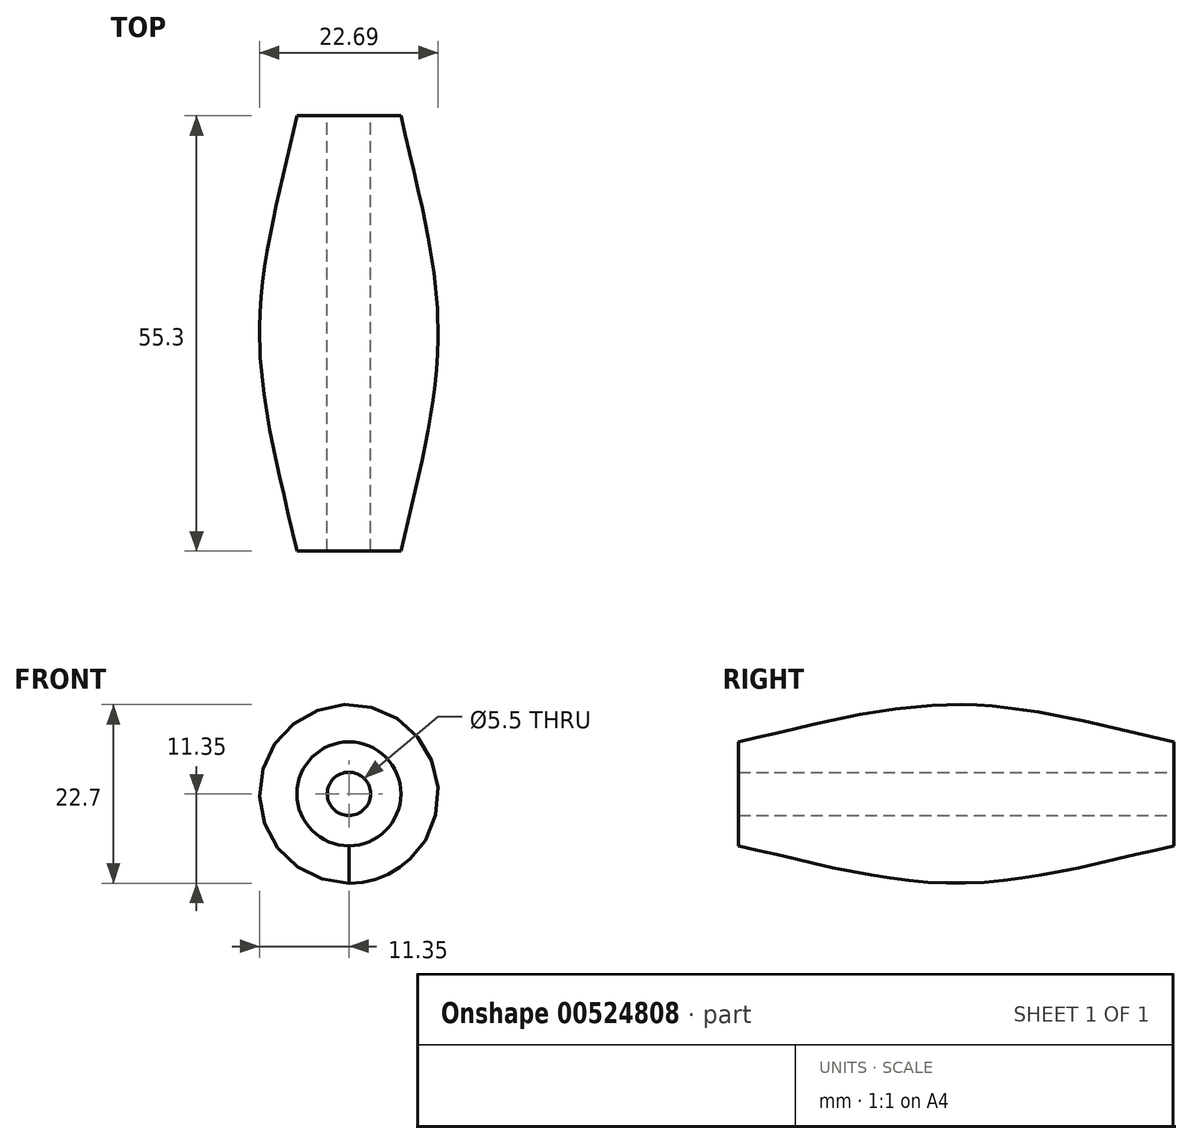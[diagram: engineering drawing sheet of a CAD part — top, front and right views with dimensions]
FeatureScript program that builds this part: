
annotation { "Feature Type Name" : "Feature", "Feature Type Description" : "" }
export const myFeature = defineFeature(function(context is Context, id is Id, definition is map)
    precondition{}
    {
        {
            assignVariable(context, id + "F0", {"name" : "length", "anyValue" : 55.3});
        }
        {
            var Q0;
            Q0=qCreatedBy(makeId("Front.planeOp"),FACE);
            var sketch = newSketch(context, id + "F1", { "sketchPlane" : qUnion([Q0])});
            skCircle(sketch, "E0", {"center": v(0, 0) * mm, "radius": 2.75 * mm});
            skSolve(sketch);
        }
        {
            var Q0;
            Q0=qCreatedBy(makeId("Right.planeOp"),FACE);
            var sketch = newSketch(context, id + "F2", { "sketchPlane" : qUnion([Q0])});
            skLineSegment(sketch, "E1.bottom", {"start": v(27.65, 6.6) * mm, "end": v(-27.65, 6.6) * mm});
            skLineSegment(sketch, "E1.top", {"start": v(27.65, -6.6) * mm, "end": v(-27.65, -6.6) * mm});
            skLineSegment(sketch, "E1.left", {"start": v(27.65, 6.6) * mm, "end": v(27.65, -6.6) * mm});
            skLineSegment(sketch, "E1.right", {"start": v(-27.65, 6.6) * mm, "end": v(-27.65, -6.6) * mm});
            skPoint(sketch, "E1.middle", {"position": v(0, 0) * mm});
            skFitSpline(sketch, "E2", {"points": [v(27.65, 6.6) * mm, v(0, 11.35) * mm, v(-27.65, 6.6) * mm], "startDerivative": vector(-55.3, 12.48) * mm, "endDerivative": vector(-55.3, -12.48) * mm});
            skLineSegment(sketch, "E3", {"start": v(-64.67, 0) * mm, "end": v(60.55, 0) * mm});
            skSolve(sketch);
        }
        {
            var Q0;
            Q0=makeQuery(id+"F2.imprint","IMPRINT",FACE,{"disambiguationData":[TD([[makeQuery(id+"F2.imprint","IMPRINT",EDGE,{"derivedFrom":sQuery(id+"F2.wireOp",EDGE,"E1.bottom")}),-1.0]])]});
            var Q1;
            {var subQ0=sQuery(id+"F2.wireOp",EDGE,"E1.bottom");Q1=makeQuery(id+"F2.imprint","IMPRINT",FACE,{"disambiguationData":[TD([[makeQuery(id+"F2.imprint","IMPRINT",EDGE,{"derivedFrom":subQ0}),1.0]])]});}
            var Q2;
            Q2=sQuery(id+"F2.wireOp",EDGE,"E3");
            revolve(context, id + "F3", {"entities" : qUnion([Q0, Q1]), "axis" : qUnion([Q2]), "revolveType" : RevolveType.FULL});
        }
        {
            var Q0;
            Q0 = qSketchRegion(id + "F1", true);
            extrude(context, id + "F4", {"entities" : qUnion([Q0]), "operationType" : NewBodyOperationType.REMOVE, "depth" : (getVariable(context, 'length') * 2) * mm, "offsetDistance" : 25 * mm, "symmetric" : true});
        }
    });
